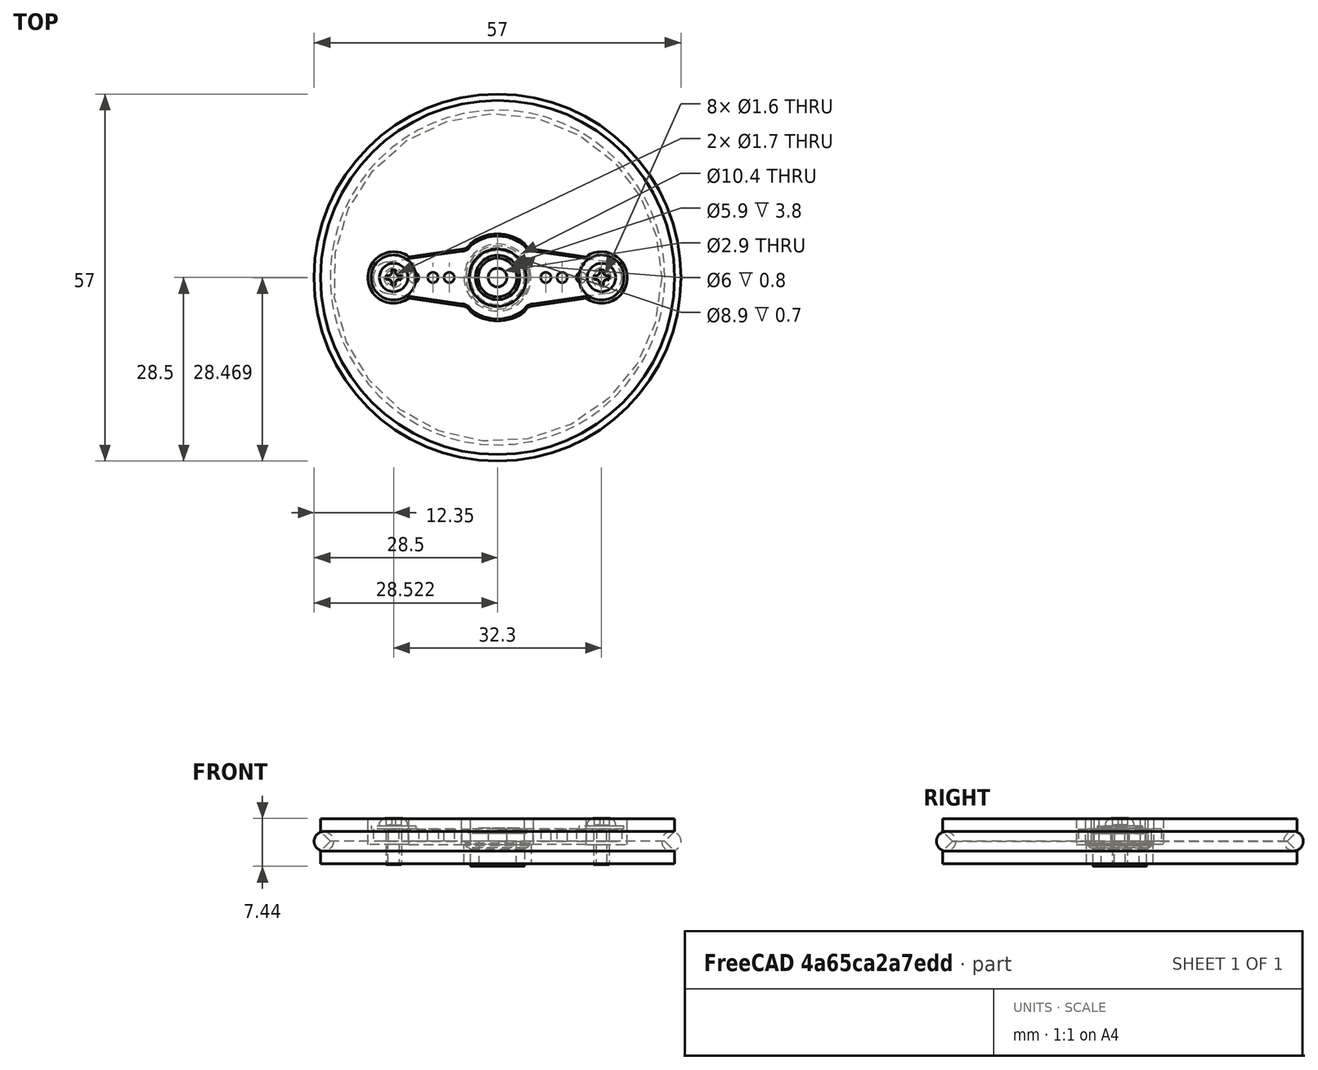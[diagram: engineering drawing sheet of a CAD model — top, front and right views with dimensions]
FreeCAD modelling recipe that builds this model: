
FCSTD DOCUMENT  (FreeCAD 0.14R3702 (Git))
Label: Renacuajo-wheel-2-arms-horn-assembly
License: CC-BY 3.0
LicenseURL: http://creativecommons.org/licenses/by/3.0/
objects: Part::Feature×4, Part::Torus×1, Part::Compound×1
note: 6 computed .brp shape members not serialized (recipe doc carries the construction recipe); baked Part::Feature solids carry a one-line shape summary decoded from their .brp

FEATURE [Part::Torus] Torus  label="o-ring"
  Angle1 = -180
  Angle2 = 180
  Angle3 = 360
  Radius1 = 27
  Radius2 = 1.5
FEATURE [Part::Feature] Chamfer  label="screw1"
  Placement = pos=(16.15,0,1.9) rot=(0,0,1;0rad)
  shape: bbox 7 x 7 x 7.14 mm, 33 faces (baked)
FEATURE [Part::Feature] Chamfer001  label="screw002"
  Placement = pos=(-16.15,0,1.9) rot=(0,0,1;0rad)
  shape: bbox 7 x 7 x 7.14 mm, 33 faces (baked)
FEATURE [Part::Feature] Chamfer002  label="horn-final002"
  shape: bbox 38.6 x 12.9 x 5.9 mm, 40 faces (baked)
FEATURE [Part::Feature] Mirrored  label="Renacuajo-wheel-2-arms-horn-final"
  shape: bbox 55 x 55 x 7 mm, 22 faces (baked)
FEATURE [Part::Compound] Compound  label="Renacuajo-wheel-2-arms-horn-assembly-final"
  Links = -> [Torus,Mirrored,Chamfer,Chamfer001,Chamfer002]
